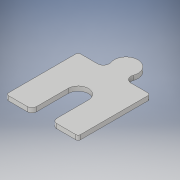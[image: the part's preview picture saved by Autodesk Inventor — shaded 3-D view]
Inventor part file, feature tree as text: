
AUTODESK INVENTOR PART (.ipt)
format: ipt  version: 2018 (Build 220112000, 112)  size: 125,440 bytes
history: native  units: in
note: dims shown in document units (in); Inventor stores cm internally (conversion verified against a paired STEP export)
features: fillet x1
ambient origin geometry x8: Origin, YZ Plane, XZ Plane, XY Plane, X Axis, Y Axis, Z Axis, Center Point
bodies: Solid1 (feature_tree)
feature tree (1):
  fillet  "Fillet2"  [1 undecoded]
note: 1 required parameter value undecoded (feature->parameter linkage not recoverable at this tier; creation-order binding heuristic only, values carry confidence <= 0.55)
